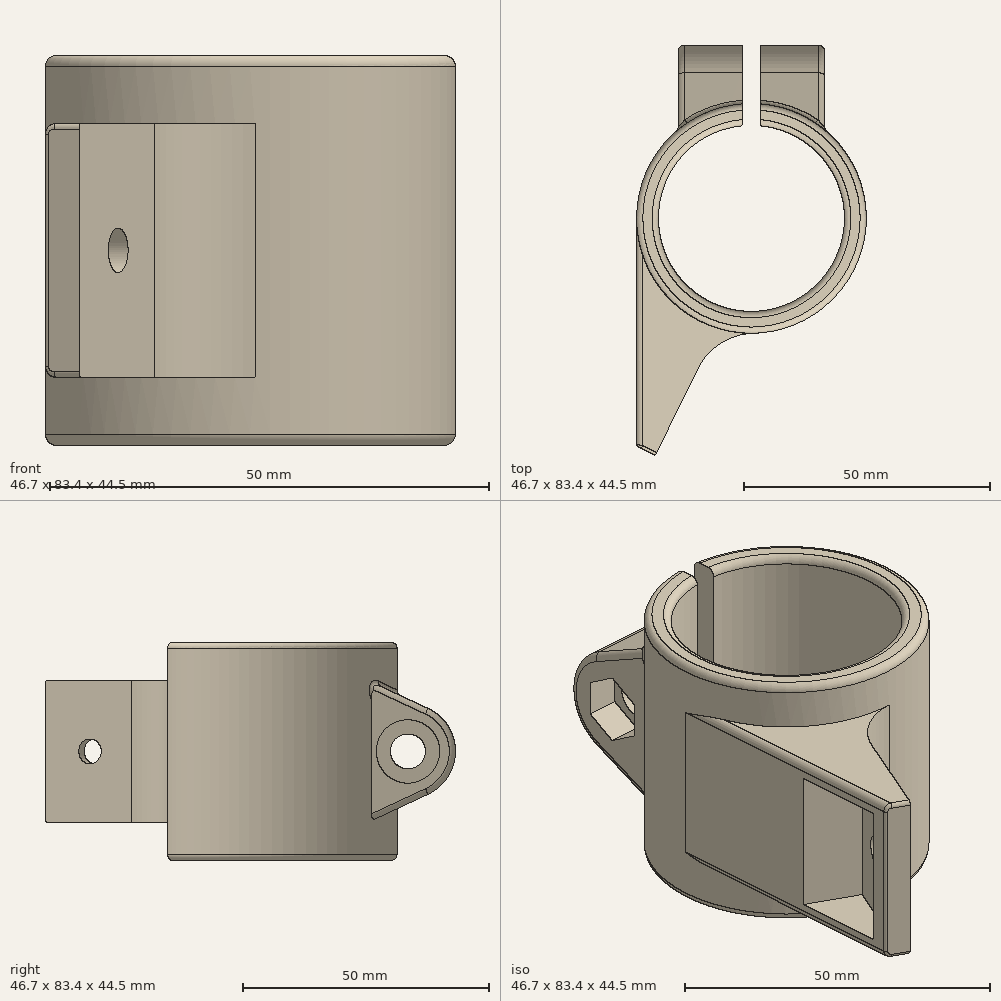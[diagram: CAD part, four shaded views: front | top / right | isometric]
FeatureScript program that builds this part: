
annotation { "Feature Type Name" : "Feature", "Feature Type Description" : "" }
export const myFeature = defineFeature(function(context is Context, id is Id, definition is map)
    precondition{}
    {
        {
            var Q0;
            Q0=qCreatedBy(makeId("Top.planeOp"),FACE);
            var sketch = newSketch(context, id + "F0", { "sketchPlane" : qUnion([Q0])});
            skCircle(sketch, "E0", {"center": v(0, 0) * mm, "radius": 23.37 * mm});
            skCircle(sketch, "E1", {"center": v(0, 0) * mm, "radius": 18.92 * mm});
            skSolve(sketch);
        }
        {
            var Q0;
            Q0 = qSketchRegion(id + "F0", true);
            extrude(context, id + "F1", {"entities" : qUnion([Q0]), "depth" : 44.45 * mm});
        }
        {
            var Q0;
            Q0=qCreatedBy(makeId("Right.planeOp"),FACE);
            var sketch = newSketch(context, id + "F2", { "sketchPlane" : qUnion([Q0])});
            skLineSegment(sketch, "E2", {"start": v(0, -0.33) * mm, "end": v(29.6, 13.48) * mm});
            skLineSegment(sketch, "E3", {"start": v(29.6, 30.97) * mm, "end": v(0, 44.78) * mm});
            skArc(sketch, "E4", {"start": v(29.6, 13.48) * mm, "mid": v(35.18, 22.23) * mm, "end": v(29.6, 30.97) * mm});
            skLineSegment(sketch, "E5", {"start": v(0, -0.33) * mm, "end": v(0, 44.78) * mm});
            skCircle(sketch, "E6", {"center": v(25.53, 22.23) * mm, "radius": 3.56 * mm});
            skLineSegment(sketch, "E7.0", {"start": v(-18.92, 44.45) * mm, "end": v(18.92, 44.45) * mm, "construction": true});
            skPoint(sketch, "E8", {"position": v(35.18, 22.23) * mm});
            skLineSegment(sketch, "E9", {"start": v(0, 0) * mm, "end": v(0, 44.45) * mm, "construction": true});
            skPoint(sketch, "E10", {"position": v(0, 22.23) * mm});
            skSolve(sketch);
        }
        {
            var Q0;
            Q0 = qSketchRegion(id + "F2", true);
            extrude(context, id + "F3", {"entities" : qUnion([Q0]), "operationType" : NewBodyOperationType.ADD, "endBound" : BoundingType.SYMMETRIC, "depth" : 29.84 * mm});
        }
        {
            var Q0;
            {var subQ0=sQuery(id+"F2.wireOp",EDGE,"E4");var subQ1=sQuery(id+"F2.wireOp",EDGE,"E2");var subQ2=sQuery(id+"F2.wireOp",EDGE,"E3");var subQ3=sQuery(id+"F2.wireOp",EDGE,"E6");Q0=makeQuery(id+"F3.boolean.opBoolean","SPLIT",FACE,{"disambiguationData":[TD([makeQuery(id+"F1.opExtrude","SWEPT_FACE",FACE,{"disambiguationData":[OSD([sQuery(id+"F0.wireOp",EDGE,"E0")])]})])],"derivedFrom":makeQuery(id+"F3.opExtrude","CAP_FACE",FACE,{"disambiguationData":[OSD([subQ1,subQ2,subQ0,sQuery(id+"F2.wireOp",EDGE,"E5"),subQ3])],"isStart":false})});}
            var sketch = newSketch(context, id + "F4", { "sketchPlane" : qUnion([Q0])});
            skCircle(sketch, "E11.0", {"center": v(25.53, 22.23) * mm, "radius": 3.56 * mm});
            skSolve(sketch);
        }
        {
            var Q0;
            Q0 = qSketchRegion(id + "F4", true);
            extrude(context, id + "F5", {"entities" : qUnion([Q0]), "operationType" : NewBodyOperationType.REMOVE, "endBound" : BoundingType.THROUGH_ALL, "oppositeDirection" : true, "depth" : 25.4 * mm});
        }
        {
            var Q0;
            Q0=makeQuery(id+"F1.opExtrude","CAP_FACE",FACE,{"disambiguationData":[OSD([sQuery(id+"F0.wireOp",EDGE,"E0"),sQuery(id+"F0.wireOp",EDGE,"E1")])],"isStart":false});
            var sketch = newSketch(context, id + "F6", { "sketchPlane" : qUnion([Q0])});
            skCircle(sketch, "E12.0", {"center": v(0, 0) * mm, "radius": 18.92 * mm});
            skLineSegment(sketch, "E13.bottom", {"start": v(-1.9, 17.3) * mm, "end": v(1.9, 17.3) * mm});
            skLineSegment(sketch, "E13.top", {"start": v(-1.9, 38.21) * mm, "end": v(1.9, 38.21) * mm});
            skLineSegment(sketch, "E13.left", {"start": v(-1.9, 17.3) * mm, "end": v(-1.9, 38.21) * mm});
            skLineSegment(sketch, "E13.right", {"start": v(1.9, 17.3) * mm, "end": v(1.9, 38.21) * mm});
            skPoint(sketch, "E14", {"position": v(0, 17.3) * mm});
            skSolve(sketch);
        }
        {
            var Q0;
            Q0 = qSketchRegion(id + "F6", true);
            extrude(context, id + "F7", {"entities" : qUnion([Q0]), "operationType" : NewBodyOperationType.REMOVE, "endBound" : BoundingType.THROUGH_ALL, "oppositeDirection" : true, "depth" : 25.4 * mm, "hasSecondDirection" : true, "secondDirectionBound" : SecondDirectionBoundingType.THROUGH_ALL, "secondDirectionOppositeDirection" : false, "secondDirectionDepth" : 25.4 * mm});
        }
        {
            var Q0;
            {var subQ0=sQuery(id+"F2.wireOp",EDGE,"E4");var subQ1=sQuery(id+"F2.wireOp",EDGE,"E2");var subQ2=sQuery(id+"F2.wireOp",EDGE,"E3");var subQ3=sQuery(id+"F2.wireOp",EDGE,"E6");Q0=makeQuery(id+"F3.boolean.opBoolean","SPLIT",FACE,{"disambiguationData":[TD([makeQuery(id+"F1.opExtrude","SWEPT_FACE",FACE,{"disambiguationData":[OSD([sQuery(id+"F0.wireOp",EDGE,"E0")])]})])],"derivedFrom":makeQuery(id+"F3.opExtrude","CAP_FACE",FACE,{"disambiguationData":[OSD([subQ1,subQ2,subQ0,sQuery(id+"F2.wireOp",EDGE,"E5"),subQ3])],"isStart":false})});}
            var sketch = newSketch(context, id + "F8", { "sketchPlane" : qUnion([Q0])});
            skCircle(sketch, "E15", {"center": v(25.53, 22.23) * mm, "radius": 6.45 * mm});
            skSolve(sketch);
        }
        {
            var Q0;
            Q0=makeQuery(id+"F8.imprint","IMPRINT",FACE,{"disambiguationData":[TD([[makeQuery(id+"F8.imprint","IMPRINT",EDGE,{"derivedFrom":sQuery(id+"F8.wireOp",EDGE,"E15")}),1.0]])]});
            var Q1;
            Q1 = qSketchRegion(id + "F8", true);
            extrude(context, id + "F9", {"entities" : qUnion([Q0, Q1]), "operationType" : NewBodyOperationType.REMOVE, "oppositeDirection" : true, "depth" : 1.27 * mm});
        }
        {
            var Q0;
            {var subQ0=sQuery(id+"F2.wireOp",EDGE,"E4");var subQ1=sQuery(id+"F2.wireOp",EDGE,"E2");var subQ2=sQuery(id+"F2.wireOp",EDGE,"E3");var subQ3=sQuery(id+"F2.wireOp",EDGE,"E6");Q0=makeQuery(id+"F3.boolean.opBoolean","SPLIT",FACE,{"disambiguationData":[TD([makeQuery(id+"F1.opExtrude","SWEPT_FACE",FACE,{"disambiguationData":[OSD([sQuery(id+"F0.wireOp",EDGE,"E0")])]})])],"derivedFrom":makeQuery(id+"F3.opExtrude","CAP_FACE",FACE,{"disambiguationData":[OSD([subQ1,subQ2,subQ0,sQuery(id+"F2.wireOp",EDGE,"E5"),subQ3])],"isStart":true})});}
            var sketch = newSketch(context, id + "F10", { "sketchPlane" : qUnion([Q0])});
            skCircle(sketch, "E16.cCircle", {"center": v(-25.53, 22.23) * mm, "radius": 5.13 * mm, "construction": true});
            skLineSegment(sketch, "E16.0", {"start": v(-30.66, 19.26) * mm, "end": v(-30.66, 25.19) * mm});
            skLineSegment(sketch, "E16.1", {"start": v(-30.66, 25.19) * mm, "end": v(-25.53, 28.15) * mm});
            skLineSegment(sketch, "E16.2", {"start": v(-25.53, 28.15) * mm, "end": v(-20.4, 25.19) * mm});
            skLineSegment(sketch, "E16.3", {"start": v(-20.4, 25.19) * mm, "end": v(-20.4, 19.26) * mm});
            skLineSegment(sketch, "E16.4", {"start": v(-20.4, 19.26) * mm, "end": v(-25.53, 16.3) * mm});
            skLineSegment(sketch, "E16.5", {"start": v(-25.53, 16.3) * mm, "end": v(-30.66, 19.26) * mm});
            skPoint(sketch, "E16.0.midPoint", {"position": v(-30.66, 22.23) * mm});
            skSolve(sketch);
        }
        {
            var Q0;
            Q0 = qSketchRegion(id + "F10", true);
            extrude(context, id + "F11", {"entities" : qUnion([Q0]), "operationType" : NewBodyOperationType.REMOVE, "oppositeDirection" : true, "depth" : 5.7 * mm});
        }
        {
            var Q0;
            Q0=makeQuery(id+"F1.opExtrude","CAP_FACE",FACE,{"disambiguationData":[OSD([sQuery(id+"F0.wireOp",EDGE,"E0"),sQuery(id+"F0.wireOp",EDGE,"E1")])],"isStart":false});
            var Q1;
            Q1=makeQuery(id+"F1.opExtrude","CAP_FACE",FACE,{"disambiguationData":[OSD([sQuery(id+"F0.wireOp",EDGE,"E0"),sQuery(id+"F0.wireOp",EDGE,"E1")])],"isStart":true});
            cPlane(context, id + "F12", {"entities" : qUnion([Q0, Q1]), "cplaneType" : CPlaneType.MID_PLANE, "offset" : 25.4 * mm, "width" : 152.4 * mm, "height" : 152.4 * mm});
        }
        {
            var Q0;
            Q0=qCreatedBy(id+"F12.planeOp",FACE);
            var sketch = newSketch(context, id + "F13", { "sketchPlane" : qUnion([Q0])});
            skLineSegment(sketch, "E17", {"start": v(-23.37, -46.33) * mm, "end": v(-23.37, 0) * mm});
            skArc(sketch, "E18", {"start": v(-23.37, 0) * mm, "mid": v(-16.33, -16.71) * mm, "end": v(0.54, -23.36) * mm});
            skLineSegment(sketch, "E19", {"start": v(-10.9, -30.67) * mm, "end": v(-19.53, -48.21) * mm});
            skLineSegment(sketch, "E20", {"start": v(-19.53, -48.21) * mm, "end": v(-27.15, -44.46) * mm, "construction": true});
            skLineSegment(sketch, "E21", {"start": v(-27.15, -44.46) * mm, "end": v(-27.15, -13.18) * mm, "construction": true});
            skLineSegment(sketch, "E22", {"start": v(-27.15, -13.18) * mm, "end": v(-10.9, -30.67) * mm, "construction": true});
            skLineSegment(sketch, "E23", {"start": v(-15.22, -39.44) * mm, "end": v(-42.02, -26.25) * mm, "construction": true});
            skArc(sketch, "E24", {"start": v(0.54, -23.36) * mm, "mid": v(-6.2, -25.41) * mm, "end": v(-10.9, -30.67) * mm});
            skLineSegment(sketch, "E25", {"start": v(-19.53, -48.21) * mm, "end": v(-23.37, -46.33) * mm});
            skSolve(sketch);
        }
        {
            var Q0;
            Q0 = qSketchRegion(id + "F13", true);
            extrude(context, id + "F14", {"entities" : qUnion([Q0]), "operationType" : NewBodyOperationType.ADD, "endBound" : BoundingType.SYMMETRIC, "depth" : 28.96 * mm});
        }
        {
            var Q0;
            Q0=makeQuery(id+"F1.opExtrude","CAP_EDGE",EDGE,{"disambiguationData":[OSD([sQuery(id+"F0.wireOp",EDGE,"E0")])],"isStart":false});
            var Q1;
            Q1=makeQuery(id+"F1.opExtrude","CAP_EDGE",EDGE,{"disambiguationData":[OSD([sQuery(id+"F0.wireOp",EDGE,"E1")])],"isStart":false});
            var Q2;
            {var subQ1=sQuery(id+"F2.wireOp",EDGE,"E3");Q2=makeQuery(id+"F3.boolean.opBoolean","SPLIT",EDGE,{"disambiguationData":[TD([makeQuery(id+"F1.opExtrude","SWEPT_FACE",FACE,{"disambiguationData":[OSD([sQuery(id+"F0.wireOp",EDGE,"E0")])]})])],"derivedFrom":makeQuery(id+"F3.opExtrude","CAP_EDGE",EDGE,{"disambiguationData":[OSD([subQ1])],"isStart":false})});}
            var Q3;
            Q3=makeQuery(id+"F3.opExtrude","CAP_EDGE",EDGE,{"disambiguationData":[OSD([sQuery(id+"F2.wireOp",EDGE,"E4")])],"isStart":true});
            var Q4;
            {var subQ0=makeQuery(id+"F1.opExtrude","SWEPT_FACE",FACE,{"disambiguationData":[OSD([sQuery(id+"F0.wireOp",EDGE,"E0")])]});var subQ1=sQuery(id+"F2.wireOp",EDGE,"E3");var subQ2=makeQuery(id+"F3.opExtrude","SWEPT_FACE",FACE,{"disambiguationData":[OSD([subQ1])]});Q4=makeQuery(id+"F7.boolean.opBoolean","SPLIT",EDGE,{"disambiguationData":[TD([makeQuery(id+"F7.opExtrude","SWEPT_FACE",FACE,{"disambiguationData":[OSD([sQuery(id+"F6.wireOp",EDGE,"E13.right")])]})])],"derivedFrom":makeQuery(id+"F3.boolean.opBoolean","INTERSECT",EDGE,{"derivedFrom":[subQ0,subQ2]})});}
            var Q5;
            {var subQ0=makeQuery(id+"F1.opExtrude","SWEPT_FACE",FACE,{"disambiguationData":[OSD([sQuery(id+"F0.wireOp",EDGE,"E0")])]});var subQ1=sQuery(id+"F2.wireOp",EDGE,"E3");var subQ2=makeQuery(id+"F3.opExtrude","SWEPT_FACE",FACE,{"disambiguationData":[OSD([subQ1])]});Q5=makeQuery(id+"F7.boolean.opBoolean","SPLIT",EDGE,{"disambiguationData":[TD([makeQuery(id+"F7.opExtrude","SWEPT_FACE",FACE,{"disambiguationData":[OSD([sQuery(id+"F6.wireOp",EDGE,"E13.left")])]})])],"derivedFrom":makeQuery(id+"F3.boolean.opBoolean","INTERSECT",EDGE,{"derivedFrom":[subQ0,subQ2]})});}
            var Q6;
            Q6=makeQuery(id+"F1.opExtrude","CAP_EDGE",EDGE,{"disambiguationData":[OSD([sQuery(id+"F0.wireOp",EDGE,"E0")])],"isStart":true});
            var Q7;
            Q7=makeQuery(id+"F1.opExtrude","CAP_EDGE",EDGE,{"disambiguationData":[OSD([sQuery(id+"F0.wireOp",EDGE,"E1")])],"isStart":true});
            var Q8;
            Q8=makeQuery(id+"F14.opExtrude","CAP_EDGE",EDGE,{"disambiguationData":[OSD([sQuery(id+"F13.wireOp",EDGE,"E18")])],"isStart":false});
            var Q9;
            Q9=makeQuery(id+"F14.opExtrude","CAP_EDGE",EDGE,{"disambiguationData":[OSD([sQuery(id+"F13.wireOp",EDGE,"E18")])],"isStart":true});
            var Q10;
            Q10=makeQuery(id+"F14.opExtrude","CAP_EDGE",EDGE,{"disambiguationData":[OSD([sQuery(id+"F13.wireOp",EDGE,"E17")])],"isStart":false});
            var Q11;
            Q11=makeQuery(id+"F14.opExtrude","CAP_EDGE",EDGE,{"disambiguationData":[OSD([sQuery(id+"F13.wireOp",EDGE,"E17")])],"isStart":true});
            fillet(context, id + "F15", {"entities" : qUnion([Q0, Q1, Q2, Q3, Q4, Q5, Q6, Q7, Q8, Q9, Q10, Q11]), "radius" : 1.27 * mm, "tangentPropagation" : true, "allowEdgeOverflow" : false});
        }
        {
            var Q0;
            Q0=makeQuery(id+"F14.opExtrude","CAP_EDGE",EDGE,{"disambiguationData":[OSD([sQuery(id+"F13.wireOp",EDGE,"E25")])],"isStart":false});
            var Q1;
            Q1=makeQuery(id+"F14.opExtrude","CAP_EDGE",EDGE,{"disambiguationData":[OSD([sQuery(id+"F13.wireOp",EDGE,"E25")])],"isStart":true});
            fillet(context, id + "F16", {"entities" : qUnion([Q0, Q1]), "radius" : 0.64 * mm, "tangentPropagation" : true, "allowEdgeOverflow" : false});
        }
        {
            var Q0;
            Q0=makeQuery(id+"F14.opExtrude","SWEPT_FACE",FACE,{"disambiguationData":[OSD([sQuery(id+"F13.wireOp",EDGE,"E19")])]});
            var sketch = newSketch(context, id + "F17", { "sketchPlane" : qUnion([Q0])});
            skCircle(sketch, "E26", {"center": v(-41.79, 22.23) * mm, "radius": 2.54 * mm});
            skSolve(sketch);
        }
        {
            var Q0;
            Q0 = qSketchRegion(id + "F17", true);
            extrude(context, id + "F18", {"entities" : qUnion([Q0]), "operationType" : NewBodyOperationType.REMOVE, "endBound" : BoundingType.THROUGH_ALL, "oppositeDirection" : true, "depth" : 25.4 * mm});
        }
        {
            var Q0;
            Q0=makeQuery(id+"F14.opExtrude","SWEPT_FACE",FACE,{"disambiguationData":[OSD([sQuery(id+"F13.wireOp",EDGE,"E19")])]});
            var sketch = newSketch(context, id + "F19", { "sketchPlane" : qUnion([Q0])});
            skLineSegment(sketch, "E27.bottom", {"start": v(-34.87, 34.16) * mm, "end": v(-49.34, 34.16) * mm});
            skLineSegment(sketch, "E27.top", {"start": v(-34.87, 10.29) * mm, "end": v(-49.34, 10.29) * mm});
            skLineSegment(sketch, "E27.left", {"start": v(-34.87, 34.16) * mm, "end": v(-34.87, 10.29) * mm});
            skLineSegment(sketch, "E27.right", {"start": v(-49.34, 34.16) * mm, "end": v(-49.34, 10.29) * mm});
            skSolve(sketch);
        }
        {
            var Q0;
            Q0 = qSketchRegion(id + "F19", true);
            extrude(context, id + "F20", {"entities" : qUnion([Q0]), "operationType" : NewBodyOperationType.REMOVE, "oppositeDirection" : true, "depth" : 25.4 * mm, "hasSecondDirection" : true, "secondDirectionOppositeDirection" : true, "secondDirectionDepth" : 2.54 * mm});
        }
    });
